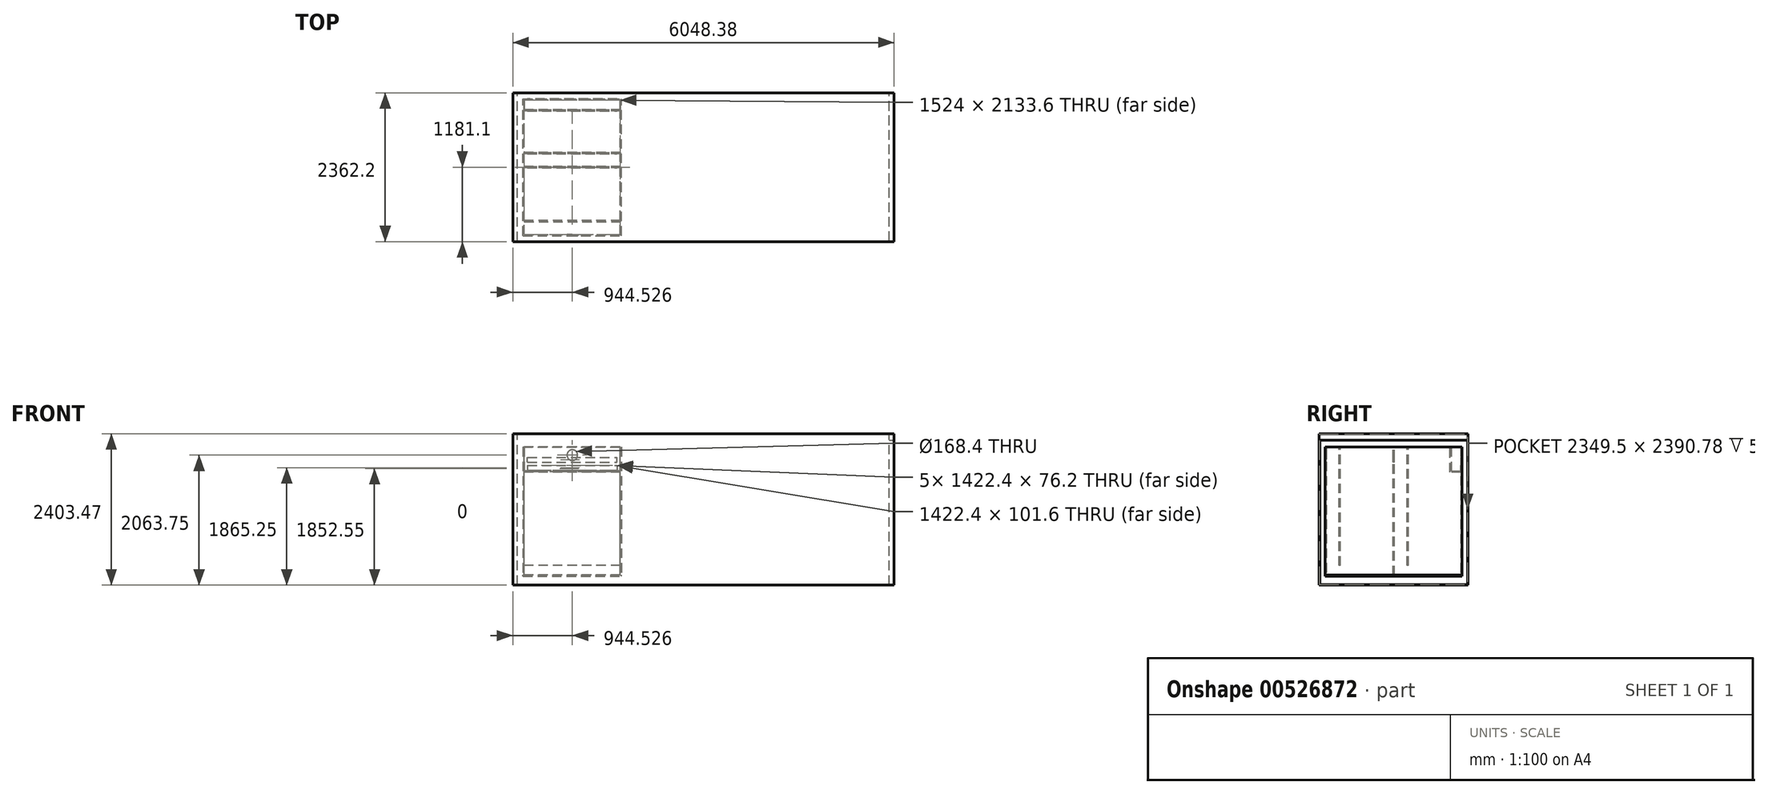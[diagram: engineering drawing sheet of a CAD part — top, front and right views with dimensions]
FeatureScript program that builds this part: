
annotation { "Feature Type Name" : "Feature", "Feature Type Description" : "" }
export const myFeature = defineFeature(function(context is Context, id is Id, definition is map)
    precondition{}
    {
        {
            var Q0;
            Q0=qCreatedBy(makeId("Right.planeOp"),FACE);
            var sketch = newSketch(context, id + "F0", { "sketchPlane" : qUnion([Q0])});
            skLineSegment(sketch, "E0.bottom", {"start": v(-1174.75, 0) * mm, "end": v(1174.75, 0) * mm});
            skLineSegment(sketch, "E0.top", {"start": v(-1174.75, 2390.78) * mm, "end": v(1174.75, 2390.78) * mm});
            skLineSegment(sketch, "E0.left", {"start": v(-1174.75, 0) * mm, "end": v(-1174.75, 2390.78) * mm});
            skLineSegment(sketch, "E0.right", {"start": v(1174.75, 0) * mm, "end": v(1174.75, 2390.78) * mm});
            skLineSegment(sketch, "E1.bottom", {"start": v(-1169.99, 0) * mm, "end": v(1169.99, 0) * mm});
            skLineSegment(sketch, "E1.top", {"start": v(-1169.99, 2292.35) * mm, "end": v(1169.99, 2292.35) * mm});
            skLineSegment(sketch, "E1.left", {"start": v(-1169.99, 0) * mm, "end": v(-1169.99, 2292.35) * mm});
            skLineSegment(sketch, "E1.right", {"start": v(1169.99, 0) * mm, "end": v(1169.99, 2292.35) * mm});
            skLineSegment(sketch, "E2.0", {"start": v(-1181.1, 2397.13) * mm, "end": v(1181.1, 2397.13) * mm});
            skLineSegment(sketch, "E2.1", {"start": v(-1181.1, -6.35) * mm, "end": v(-1181.1, 2397.13) * mm});
            skLineSegment(sketch, "E2.2", {"start": v(-1181.1, -6.35) * mm, "end": v(1181.1, -6.35) * mm});
            skLineSegment(sketch, "E2.3", {"start": v(1181.1, -6.35) * mm, "end": v(1181.1, 2397.13) * mm});
            skSolve(sketch);
        }
        {
            var Q0;
            Q0=makeQuery(id+"F0.imprint","IMPRINT",FACE,{"disambiguationData":[TD([[makeQuery(id+"F0.imprint","IMPRINT",EDGE,{"derivedFrom":sQuery(id+"F0.wireOp",EDGE,"E0.top")}),1.0]])]});
            extrude(context, id + "F1", {"entities" : qUnion([Q0]), "oppositeDirection" : true, "depth" : 6048.38 * mm, "offsetDistance" : 25.4 * mm});
        }
        {
            var Q0;
            Q0=makeQuery(id+"F0.imprint","IMPRINT",FACE,{"disambiguationData":[TD([[makeQuery(id+"F0.imprint","IMPRINT",EDGE,{"derivedFrom":sQuery(id+"F0.wireOp",EDGE,"E0.top")}),-1.0]])]});
            extrude(context, id + "F2", {"entities" : qUnion([Q0]), "operationType" : NewBodyOperationType.ADD, "oppositeDirection" : true, "depth" : 76.2 * mm, "offsetDistance" : 25.4 * mm});
        }
        {
            var Q0;
            Q0=makeQuery(id+"F1.opExtrude","CAP_FACE",FACE,{"disambiguationData":[OSD([sQuery(id+"F0.wireOp",EDGE,"E0.bottom"),sQuery(id+"F0.wireOp",EDGE,"E0.top"),sQuery(id+"F0.wireOp",EDGE,"E0.left"),sQuery(id+"F0.wireOp",EDGE,"E0.right"),sQuery(id+"F0.wireOp",EDGE,"E1.bottom"),sQuery(id+"F0.wireOp",EDGE,"E2.0"),sQuery(id+"F0.wireOp",EDGE,"E2.1"),sQuery(id+"F0.wireOp",EDGE,"E2.2"),sQuery(id+"F0.wireOp",EDGE,"E2.3")])],"isStart":false});
            var sketch = newSketch(context, id + "F3", { "sketchPlane" : qUnion([Q0])});
            skLineSegment(sketch, "E3.0", {"start": v(-1174.75, 0) * mm, "end": v(-1174.75, 2390.78) * mm});
            skLineSegment(sketch, "E4.0", {"start": v(1174.75, 2390.78) * mm, "end": v(-1174.75, 2390.78) * mm});
            skLineSegment(sketch, "E5.0", {"start": v(1174.75, 0) * mm, "end": v(-1174.75, 0) * mm});
            skLineSegment(sketch, "E6.0", {"start": v(1174.75, 0) * mm, "end": v(1174.75, 2390.78) * mm});
            skSolve(sketch);
        }
        {
            var Q0;
            Q0=makeQuery(id+"F3.imprint","IMPRINT",FACE,{"disambiguationData":[TD([[makeQuery(id+"F3.imprint","IMPRINT",EDGE,{"derivedFrom":sQuery(id+"F3.wireOp",EDGE,"E3.0")}),-1.0]])]});
            extrude(context, id + "F4", {"entities" : qUnion([Q0]), "operationType" : NewBodyOperationType.ADD, "oppositeDirection" : true, "depth" : 76.2 * mm, "offsetDistance" : 25.4 * mm});
        }
        {
            var Q0;
            Q0=qCreatedBy(makeId("Top.planeOp"),FACE);
            var sketch = newSketch(context, id + "F5", { "sketchPlane" : qUnion([Q0])});
            skLineSegment(sketch, "E7.bottom", {"start": v(-5865.85, -1066.8) * mm, "end": v(-4341.85, -1066.8) * mm});
            skLineSegment(sketch, "E7.top", {"start": v(-5865.85, 1066.8) * mm, "end": v(-4341.85, 1066.8) * mm});
            skLineSegment(sketch, "E7.left", {"start": v(-5865.85, -1066.8) * mm, "end": v(-5865.85, 1066.8) * mm});
            skLineSegment(sketch, "E7.right", {"start": v(-4341.85, -1066.8) * mm, "end": v(-4341.85, 1066.8) * mm});
            skLineSegment(sketch, "E8.0", {"start": v(-5884.9, -1085.85) * mm, "end": v(-5884.9, 1085.85) * mm});
            skLineSegment(sketch, "E8.1", {"start": v(-5884.9, -1085.85) * mm, "end": v(-4322.8, -1085.85) * mm});
            skLineSegment(sketch, "E8.2", {"start": v(-4322.8, -1085.85) * mm, "end": v(-4322.8, 1085.85) * mm});
            skLineSegment(sketch, "E8.3", {"start": v(-5884.9, 1085.85) * mm, "end": v(-4322.8, 1085.85) * mm});
            skLineSegment(sketch, "E9", {"start": v(-5075.3, -1085.85) * mm, "end": v(-5075.3, -1174.75) * mm, "construction": true});
            skLineSegment(sketch, "E10", {"start": v(-5144.4, 1085.85) * mm, "end": v(-5144.4, 1174.75) * mm, "construction": true});
            skSolve(sketch);
        }
        {
            var Q0;
            Q0=makeQuery(id+"F5.imprint","IMPRINT",FACE,{"disambiguationData":[TD([[makeQuery(id+"F5.imprint","IMPRINT",EDGE,{"derivedFrom":sQuery(id+"F5.wireOp",EDGE,"E7.bottom")}),-1.0]])]});
            extrude(context, id + "F6", {"entities" : qUnion([Q0]), "depth" : 2032 * mm, "offsetDistance" : 25.4 * mm});
        }
        {
            var Q0;
            Q0=makeQuery(id+"F6.opExtrude","CAP_FACE",FACE,{"disambiguationData":[OSD([sQuery(id+"F5.wireOp",EDGE,"E7.bottom"),sQuery(id+"F5.wireOp",EDGE,"E7.top"),sQuery(id+"F5.wireOp",EDGE,"E7.left"),sQuery(id+"F5.wireOp",EDGE,"E7.right")])],"isStart":false});
            var sketch = newSketch(context, id + "F7", { "sketchPlane" : qUnion([Q0])});
            skLineSegment(sketch, "E11.bottom", {"start": v(-4341.85, -863.6) * mm, "end": v(-5865.85, -863.6) * mm});
            skLineSegment(sketch, "E11.top", {"start": v(-5865.85, -844.55) * mm, "end": v(-4341.85, -844.55) * mm});
            skLineSegment(sketch, "E11.left", {"start": v(-5865.85, -863.6) * mm, "end": v(-5865.85, -844.55) * mm});
            skLineSegment(sketch, "E11.right", {"start": v(-4341.85, -863.6) * mm, "end": v(-4341.85, -844.55) * mm});
            skLineSegment(sketch, "E12.bottom", {"start": v(-5865.85, -9.53) * mm, "end": v(-4341.85, -9.53) * mm});
            skLineSegment(sketch, "E12.top", {"start": v(-5865.85, 9.52) * mm, "end": v(-4341.85, 9.53) * mm});
            skLineSegment(sketch, "E12.left", {"start": v(-5865.85, -9.53) * mm, "end": v(-5865.85, 9.52) * mm});
            skLineSegment(sketch, "E12.right", {"start": v(-4341.85, -9.53) * mm, "end": v(-4341.85, 9.53) * mm});
            skLineSegment(sketch, "E13.bottom", {"start": v(-5865.85, 212.72) * mm, "end": v(-4341.85, 212.73) * mm});
            skLineSegment(sketch, "E13.top", {"start": v(-5865.85, 231.77) * mm, "end": v(-4341.85, 231.78) * mm});
            skLineSegment(sketch, "E13.left", {"start": v(-5865.85, 212.72) * mm, "end": v(-5865.85, 231.77) * mm});
            skLineSegment(sketch, "E13.right", {"start": v(-4341.85, 212.73) * mm, "end": v(-4341.85, 231.78) * mm});
            skLineSegment(sketch, "E14.bottom", {"start": v(-4341.85, 844.55) * mm, "end": v(-5865.85, 844.55) * mm});
            skLineSegment(sketch, "E14.top", {"start": v(-4341.85, 863.6) * mm, "end": v(-5865.85, 863.6) * mm});
            skLineSegment(sketch, "E14.left", {"start": v(-5865.85, 863.6) * mm, "end": v(-5865.85, 844.55) * mm});
            skLineSegment(sketch, "E14.right", {"start": v(-4341.85, 863.6) * mm, "end": v(-4341.85, 844.55) * mm});
            skSolve(sketch);
        }
        {
            var Q0;
            Q0=makeQuery(id+"F7.imprint","IMPRINT",FACE,{"disambiguationData":[TD([[makeQuery(id+"F7.imprint","IMPRINT",EDGE,{"derivedFrom":sQuery(id+"F7.wireOp",EDGE,"E13.bottom")}),1.0]])]});
            var Q1;
            Q1=makeQuery(id+"F7.imprint","IMPRINT",FACE,{"disambiguationData":[TD([[makeQuery(id+"F7.imprint","IMPRINT",EDGE,{"derivedFrom":sQuery(id+"F7.wireOp",EDGE,"E11.bottom")}),-1.0]])]});
            var Q2;
            Q2=makeQuery(id+"F6.opExtrude","CAP_FACE",FACE,{"disambiguationData":[OSD([sQuery(id+"F5.wireOp",EDGE,"E7.bottom"),sQuery(id+"F5.wireOp",EDGE,"E7.top"),sQuery(id+"F5.wireOp",EDGE,"E7.left"),sQuery(id+"F5.wireOp",EDGE,"E7.right"),sQuery(id+"F5.wireOp",EDGE,"E8.0"),sQuery(id+"F5.wireOp",EDGE,"E8.1"),sQuery(id+"F5.wireOp",EDGE,"E8.2"),sQuery(id+"F5.wireOp",EDGE,"E8.3")])],"isStart":true});
            extrude(context, id + "F8", {"entities" : qUnion([Q0, Q1]), "endBound" : BoundingType.UP_TO_SURFACE, "oppositeDirection" : true, "depth" : 1828.8 * mm, "endBoundEntityFace" : qUnion([Q2]), "hasOffset" : true, "offsetDistance" : 152.4 * mm});
        }
        {
            var Q0;
            Q0=makeQuery(id+"F7.imprint","IMPRINT",FACE,{"disambiguationData":[TD([[makeQuery(id+"F7.imprint","IMPRINT",EDGE,{"derivedFrom":sQuery(id+"F7.wireOp",EDGE,"E12.bottom")}),1.0]])]});
            var Q1;
            Q1=makeQuery(id+"F6.opExtrude","CAP_FACE",FACE,{"disambiguationData":[OSD([sQuery(id+"F5.wireOp",EDGE,"E7.bottom"),sQuery(id+"F5.wireOp",EDGE,"E7.top"),sQuery(id+"F5.wireOp",EDGE,"E7.left"),sQuery(id+"F5.wireOp",EDGE,"E7.right")])],"isStart":true});
            extrude(context, id + "F9", {"entities" : qUnion([Q0]), "endBound" : BoundingType.UP_TO_SURFACE, "oppositeDirection" : true, "depth" : 25.4 * mm, "endBoundEntityFace" : qUnion([Q1]), "offsetDistance" : 25.4 * mm});
        }
        {
            var Q0;
            Q0=makeQuery(id+"F5.imprint","IMPRINT",FACE,{"disambiguationData":[TD([[makeQuery(id+"F5.imprint","IMPRINT",EDGE,{"derivedFrom":sQuery(id+"F5.wireOp",EDGE,"E7.bottom")}),1.0]])]});
            var Q1;
            Q1=makeQuery(id+"F5.imprint","IMPRINT",FACE,{"disambiguationData":[TD([[makeQuery(id+"F5.imprint","IMPRINT",EDGE,{"derivedFrom":sQuery(id+"F5.wireOp",EDGE,"E7.bottom")}),-1.0]])]});
            extrude(context, id + "F10", {"entities" : qUnion([Q0, Q1]), "oppositeDirection" : true, "depth" : 19.05 * mm, "offsetDistance" : 25.4 * mm});
        }
        {
            var Q0;
            Q0=makeQuery(id+"F6.opExtrude","SWEPT_FACE",FACE,{"disambiguationData":[OSD([sQuery(id+"F5.wireOp",EDGE,"E8.2")])]});
            var Q1;
            Q1=makeQuery(id+"F6.opExtrude","SWEPT_FACE",FACE,{"disambiguationData":[OSD([sQuery(id+"F5.wireOp",EDGE,"E8.0")])]});
            cPlane(context, id + "F11", {"entities" : qUnion([Q0, Q1]), "cplaneType" : CPlaneType.MID_PLANE, "offset" : 25.4 * mm, "width" : 152.4 * mm, "height" : 152.4 * mm});
        }
        {
            var Q0;
            Q0=makeQuery(id+"F6.opExtrude","SWEPT_FACE",FACE,{"disambiguationData":[OSD([sQuery(id+"F5.wireOp",EDGE,"E8.1")])]});
            var sketch = newSketch(context, id + "F12", { "sketchPlane" : qUnion([Q0])});
            skCircle(sketch, "E15", {"center": v(-5103.85, 1905) * mm, "radius": 84.2 * mm});
            skSolve(sketch);
        }
        {
            var Q0;
            Q0=makeQuery(id+"F12.imprint","IMPRINT",FACE,{"disambiguationData":[TD([[makeQuery(id+"F12.imprint","IMPRINT",EDGE,{"derivedFrom":sQuery(id+"F12.wireOp",EDGE,"E15")}),1.0]])]});
            extrude(context, id + "F13", {"entities" : qUnion([Q0]), "operationType" : NewBodyOperationType.REMOVE, "endBound" : BoundingType.UP_TO_NEXT, "oppositeDirection" : true, "depth" : 25.4 * mm, "offsetDistance" : 25.4 * mm});
        }
        {
            var Q0;
            Q0=makeQuery(id+"F9.opExtrude","SWEPT_FACE",FACE,{"disambiguationData":[OSD([sQuery(id+"F7.wireOp",EDGE,"E12.bottom")])]});
            var sketch = newSketch(context, id + "F14", { "sketchPlane" : qUnion([Q0])});
            skLineSegment(sketch, "E16.bottom", {"start": v(-5815.05, 1795.4) * mm, "end": v(-4392.65, 1795.4) * mm});
            skLineSegment(sketch, "E16.top", {"start": v(-5815.05, 1871.6) * mm, "end": v(-4392.65, 1871.6) * mm});
            skLineSegment(sketch, "E16.left", {"start": v(-5815.05, 1795.4) * mm, "end": v(-5815.05, 1871.6) * mm});
            skLineSegment(sketch, "E16.right", {"start": v(-4392.65, 1795.4) * mm, "end": v(-4392.65, 1871.6) * mm});
            skCircle(sketch, "E17.0", {"center": v(-5103.85, 1905) * mm, "radius": 84.2 * mm, "construction": true});
            skSolve(sketch);
        }
        {
            var Q0;
            Q0=makeQuery(id+"F14.imprint","IMPRINT",FACE,{"disambiguationData":[TD([[makeQuery(id+"F14.imprint","IMPRINT",EDGE,{"derivedFrom":sQuery(id+"F14.wireOp",EDGE,"E16.bottom")}),1.0]])]});
            extrude(context, id + "F15", {"entities" : qUnion([Q0]), "operationType" : NewBodyOperationType.REMOVE, "endBound" : BoundingType.THROUGH_ALL, "oppositeDirection" : true, "depth" : 25.4 * mm, "offsetDistance" : 25.4 * mm});
        }
        {
            var Q0;
            Q0=makeQuery(id+"F1.opExtrude","SWEPT_BODY",BODY,{"disambiguationData":[OSD([sQuery(id+"F0.wireOp",EDGE,"E0.bottom"),sQuery(id+"F0.wireOp",EDGE,"E0.top"),sQuery(id+"F0.wireOp",EDGE,"E0.left"),sQuery(id+"F0.wireOp",EDGE,"E0.right"),sQuery(id+"F0.wireOp",EDGE,"E1.bottom"),sQuery(id+"F0.wireOp",EDGE,"E2.0"),sQuery(id+"F0.wireOp",EDGE,"E2.1"),sQuery(id+"F0.wireOp",EDGE,"E2.2"),sQuery(id+"F0.wireOp",EDGE,"E2.3")])]});
            transform(context, id + "F16", {"entities" : qUnion([Q0]), "transformType" : TransformType.TRANSLATION_3D, "dx" : 0 * mm, "dy" : 0 * mm, "dz" : -152.4 * mm, "makeCopy" : false});
        }
        {
            var Q0;
            Q0=makeQuery(id+"F6.opExtrude","SWEPT_FACE",FACE,{"disambiguationData":[OSD([sQuery(id+"F5.wireOp",EDGE,"E7.left")])]});
            var sketch = newSketch(context, id + "F17", { "sketchPlane" : qUnion([Q0])});
            skPoint(sketch, "E18.0", {"position": v(9.52, 1795.4) * mm});
            skLineSegment(sketch, "E19", {"start": v(9.52, 1795.4) * mm, "end": v(1066.8, 1795.4) * mm, "construction": true});
            skLineSegment(sketch, "E20", {"start": v(895.35, 2032) * mm, "end": v(895.35, 1631.95) * mm});
            skLineSegment(sketch, "E21", {"start": v(895.35, 1631.95) * mm, "end": v(1066.8, 1631.95) * mm});
            skLineSegment(sketch, "E22", {"start": v(1066.8, 1631.95) * mm, "end": v(1066.8, 1651) * mm});
            skLineSegment(sketch, "E23", {"start": v(1066.8, 1651) * mm, "end": v(914.4, 1651) * mm});
            skLineSegment(sketch, "E24", {"start": v(914.4, 1651) * mm, "end": v(914.4, 2032) * mm});
            skLineSegment(sketch, "E25", {"start": v(914.4, 2032) * mm, "end": v(895.35, 2032) * mm});
            skSolve(sketch);
        }
        {
            var Q0;
            Q0=makeQuery(id+"F17.imprint","IMPRINT",FACE,{"disambiguationData":[TD([[makeQuery(id+"F17.imprint","IMPRINT",EDGE,{"derivedFrom":sQuery(id+"F17.wireOp",EDGE,"E20")}),1.0]])]});
            extrude(context, id + "F18", {"entities" : qUnion([Q0]), "endBound" : BoundingType.UP_TO_NEXT, "depth" : 25.4 * mm, "offsetDistance" : 25.4 * mm});
        }
        {
            var Q0;
            Q0=makeQuery(id+"F18.opExtrude","SWEPT_FACE",FACE,{"disambiguationData":[OSD([sQuery(id+"F17.wireOp",EDGE,"E20")])]});
            var sketch = newSketch(context, id + "F19", { "sketchPlane" : qUnion([Q0])});
            skLineSegment(sketch, "E26.0", {"start": v(-5815.05, 1795.4) * mm, "end": v(-4392.65, 1795.4) * mm, "construction": true});
            skLineSegment(sketch, "E27.bottom", {"start": v(-5815.05, 1744.6) * mm, "end": v(-4392.65, 1744.6) * mm});
            skLineSegment(sketch, "E27.top", {"start": v(-5815.05, 1668.4) * mm, "end": v(-4392.65, 1668.4) * mm});
            skLineSegment(sketch, "E27.left", {"start": v(-5815.05, 1744.6) * mm, "end": v(-5815.05, 1668.4) * mm});
            skLineSegment(sketch, "E27.right", {"start": v(-4392.65, 1744.6) * mm, "end": v(-4392.65, 1668.4) * mm});
            skSolve(sketch);
        }
        {
            var Q0;
            Q0=makeQuery(id+"F19.imprint","IMPRINT",FACE,{"disambiguationData":[TD([[makeQuery(id+"F19.imprint","IMPRINT",EDGE,{"derivedFrom":sQuery(id+"F19.wireOp",EDGE,"E27.bottom")}),-1.0]])]});
            extrude(context, id + "F20", {"entities" : qUnion([Q0]), "operationType" : NewBodyOperationType.REMOVE, "endBound" : BoundingType.THROUGH_ALL, "oppositeDirection" : true, "depth" : 25.4 * mm, "offsetDistance" : 25.4 * mm});
        }
        {
            var Q0;
            Q0=makeQuery(id+"F6.opExtrude","SWEPT_FACE",FACE,{"disambiguationData":[OSD([sQuery(id+"F5.wireOp",EDGE,"E8.3")])]});
            var sketch = newSketch(context, id + "F21", { "sketchPlane" : qUnion([Q0])});
            skCircle(sketch, "E28.0", {"center": v(5103.85, 1905) * mm, "radius": 84.2 * mm, "construction": true});
            skCircle(sketch, "E29", {"center": v(5103.85, 1854.2) * mm, "radius": 84.2 * mm});
            skLineSegment(sketch, "E30.0", {"start": v(5815.05, 1795.4) * mm, "end": v(4392.65, 1795.4) * mm, "construction": true});
            skLineSegment(sketch, "E31.0", {"start": v(5815.05, 1744.6) * mm, "end": v(4392.65, 1744.6) * mm, "construction": true});
            skSolve(sketch);
        }
        {
            var Q0;
            Q0=makeQuery(id+"F21.imprint","IMPRINT",FACE,{"disambiguationData":[TD([[makeQuery(id+"F21.imprint","IMPRINT",EDGE,{"derivedFrom":sQuery(id+"F21.wireOp",EDGE,"E29")}),1.0]])]});
            extrude(context, id + "F22", {"entities" : qUnion([Q0]), "operationType" : NewBodyOperationType.REMOVE, "endBound" : BoundingType.UP_TO_NEXT, "oppositeDirection" : true, "depth" : 25.4 * mm, "offsetDistance" : 25.4 * mm});
        }
    });
